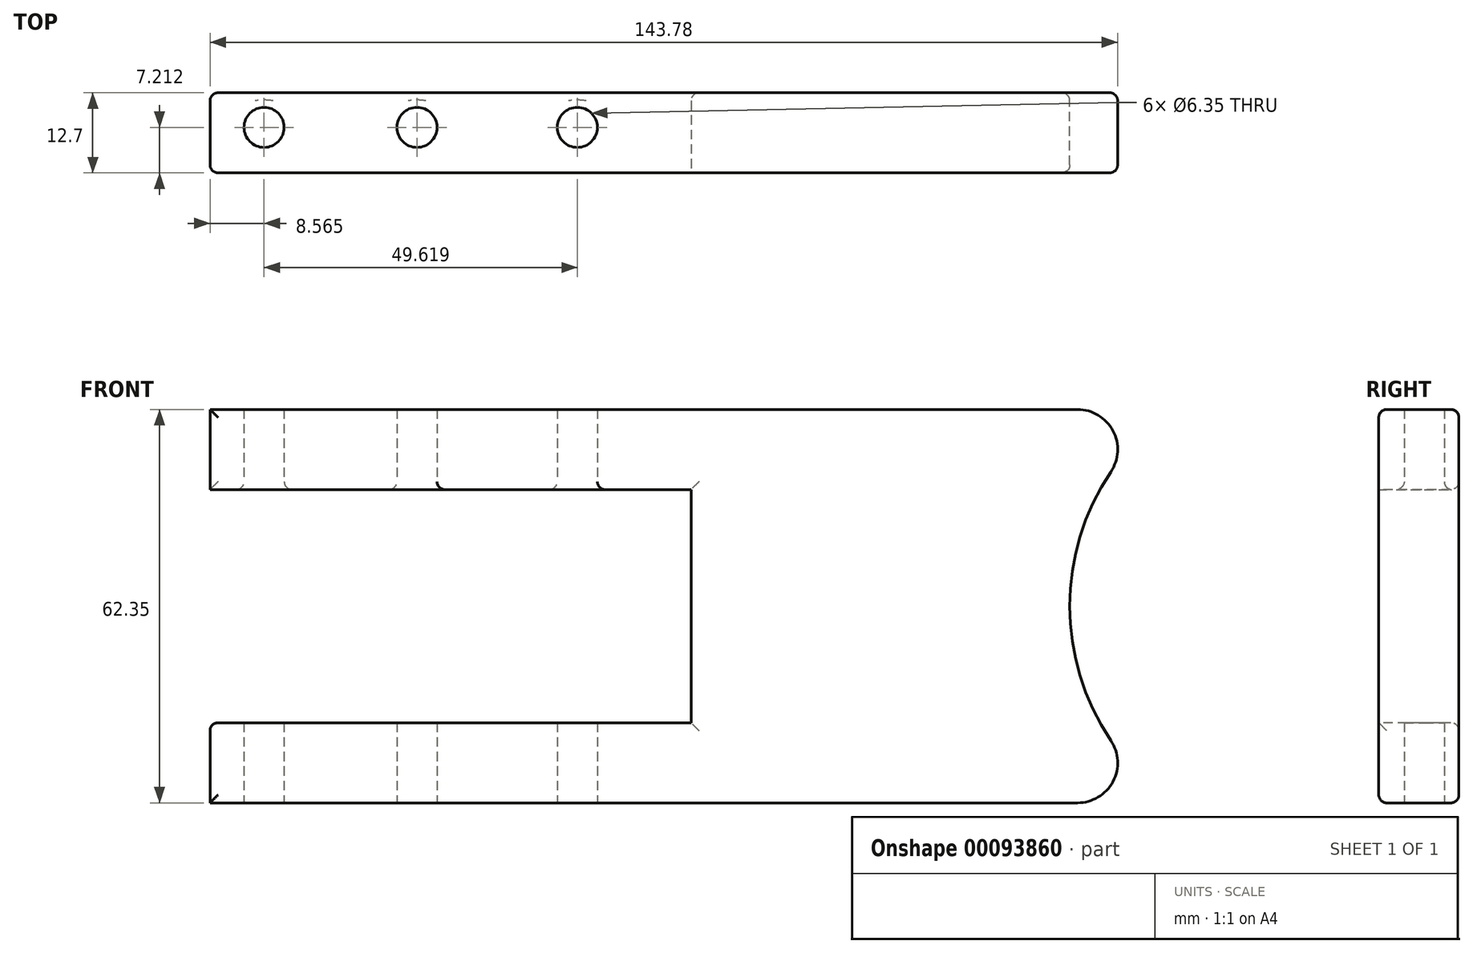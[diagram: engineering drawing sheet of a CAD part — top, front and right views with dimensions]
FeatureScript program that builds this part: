
annotation { "Feature Type Name" : "Feature", "Feature Type Description" : "" }
export const myFeature = defineFeature(function(context is Context, id is Id, definition is map)
    precondition{}
    {
        {
            var Q0;
            Q0=qCreatedBy(makeId("Front.planeOp"),FACE);
            var sketch = newSketch(context, id + "F0", { "sketchPlane" : qUnion([Q0])});
            skLineSegment(sketch, "E0.bottom", {"start": v(0, 62.35) * mm, "end": v(152.4, 62.35) * mm});
            skLineSegment(sketch, "E0.top", {"start": v(0, 0) * mm, "end": v(152.4, 0) * mm});
            skLineSegment(sketch, "E0.left", {"start": v(0, 62.35) * mm, "end": v(0, 0) * mm});
            skArc(sketch, "E1", {"start": v(152.4, 62.35) * mm, "mid": v(136.2, 31.18) * mm, "end": v(152.4, 0) * mm});
            skSolve(sketch);
        }
        {
            var Q0;
            Q0 = qSketchRegion(id + "F0", true);
            extrude(context, id + "F1", {"entities" : qUnion([Q0]), "depth" : 12.7 * mm});
        }
        {
            var Q0;
            Q0=makeQuery(id+"F1.opExtrude","SWEPT_EDGE",EDGE,{"disambiguationData":[OSD([sQuery(id+"F0.wireOp",EDGE,"E0.bottom"),sQuery(id+"F0.wireOp",EDGE,"E1")])]});
            var Q1;
            Q1=makeQuery(id+"F1.opExtrude","SWEPT_EDGE",EDGE,{"disambiguationData":[OSD([sQuery(id+"F0.wireOp",EDGE,"E0.top"),sQuery(id+"F0.wireOp",EDGE,"E1")])]});
            fillet(context, id + "F2", {"entities" : qUnion([Q0, Q1]), "radius" : 6.35 * mm, "tangentPropagation" : true, "allowEdgeOverflow" : false});
        }
        {
            var Q0;
            Q0=makeQuery(id+"F1.opExtrude","CAP_FACE",FACE,{"disambiguationData":[OSD([sQuery(id+"F0.wireOp",EDGE,"E0.bottom"),sQuery(id+"F0.wireOp",EDGE,"E0.top"),sQuery(id+"F0.wireOp",EDGE,"E0.left"),sQuery(id+"F0.wireOp",EDGE,"E1")])],"isStart":false});
            var sketch = newSketch(context, id + "F3", { "sketchPlane" : qUnion([Q0])});
            skLineSegment(sketch, "E2", {"start": v(0, 62.35) * mm, "end": v(0, 49.65) * mm});
            skLineSegment(sketch, "E3", {"start": v(0, 0) * mm, "end": v(0, 12.7) * mm});
            skLineSegment(sketch, "E4.bottom", {"start": v(0, 49.65) * mm, "end": v(76.2, 49.65) * mm});
            skLineSegment(sketch, "E4.top", {"start": v(0, 12.7) * mm, "end": v(76.2, 12.7) * mm});
            skLineSegment(sketch, "E4.left", {"start": v(0, 49.65) * mm, "end": v(0, 12.7) * mm});
            skLineSegment(sketch, "E4.right", {"start": v(76.2, 49.65) * mm, "end": v(76.2, 12.7) * mm});
            skSolve(sketch);
        }
        {
            var Q0;
            Q0=makeQuery(id+"F3.imprint","IMPRINT",FACE,{"disambiguationData":[TD([[makeQuery(id+"F3.imprint","IMPRINT",EDGE,{"derivedFrom":sQuery(id+"F3.wireOp",EDGE,"E4.bottom")}),-1.0]])]});
            extrude(context, id + "F4", {"entities" : qUnion([Q0]), "operationType" : NewBodyOperationType.REMOVE, "endBound" : BoundingType.THROUGH_ALL, "oppositeDirection" : true, "depth" : 25.4 * mm});
        }
        {
            var Q0;
            Q0=makeQuery(id+"F1.opExtrude","SWEPT_FACE",FACE,{"disambiguationData":[OSD([sQuery(id+"F0.wireOp",EDGE,"E0.top")])]});
            var sketch = newSketch(context, id + "F5", { "sketchPlane" : qUnion([Q0])});
            skCircle(sketch, "E5", {"center": v(8.57, 5.49) * mm, "radius": 3.18 * mm});
            skCircle(sketch, "E6", {"center": v(32.78, 5.49) * mm, "radius": 3.18 * mm});
            skCircle(sketch, "E7", {"center": v(58.18, 5.49) * mm, "radius": 3.18 * mm});
            skSolve(sketch);
        }
        {
            var Q0;
            Q0=makeQuery(id+"F5.imprint","IMPRINT",FACE,{"disambiguationData":[TD([[makeQuery(id+"F5.imprint","IMPRINT",EDGE,{"derivedFrom":sQuery(id+"F5.wireOp",EDGE,"E7")}),1.0]])]});
            var Q1;
            Q1=makeQuery(id+"F5.imprint","IMPRINT",FACE,{"disambiguationData":[TD([[makeQuery(id+"F5.imprint","IMPRINT",EDGE,{"derivedFrom":sQuery(id+"F5.wireOp",EDGE,"E6")}),1.0]])]});
            var Q2;
            Q2=makeQuery(id+"F5.imprint","IMPRINT",FACE,{"disambiguationData":[TD([[makeQuery(id+"F5.imprint","IMPRINT",EDGE,{"derivedFrom":sQuery(id+"F5.wireOp",EDGE,"E5")}),1.0]])]});
            extrude(context, id + "F6", {"entities" : qUnion([Q0, Q1, Q2]), "operationType" : NewBodyOperationType.REMOVE, "endBound" : BoundingType.THROUGH_ALL, "oppositeDirection" : true, "depth" : 25.4 * mm});
        }
        {
            var Q0;
            Q0=makeQuery(id+"F1.opExtrude","CAP_EDGE",EDGE,{"disambiguationData":[OSD([sQuery(id+"F0.wireOp",EDGE,"E0.bottom")])],"isStart":false});
            var Q1;
            Q1=makeQuery(id+"F6.boolean.opBoolean","COPY",EDGE,{"derivedFrom":makeQuery(id+"F6.opExtrude","CAP_EDGE",EDGE,{"disambiguationData":[OSD([sQuery(id+"F5.wireOp",EDGE,"E7")])],"isStart":true})});
            var Q2;
            Q2=makeQuery(id+"F6.boolean.opBoolean","COPY",EDGE,{"derivedFrom":makeQuery(id+"F6.opExtrude","CAP_EDGE",EDGE,{"disambiguationData":[OSD([sQuery(id+"F5.wireOp",EDGE,"E6")])],"isStart":true})});
            var Q3;
            Q3=makeQuery(id+"F6.boolean.opBoolean","COPY",EDGE,{"derivedFrom":makeQuery(id+"F6.opExtrude","CAP_EDGE",EDGE,{"disambiguationData":[OSD([sQuery(id+"F5.wireOp",EDGE,"E5")])],"isStart":true})});
            var Q4;
            Q4=makeQuery(id+"F6.boolean.opBoolean","INTERSECT",EDGE,{"derivedFrom":[makeQuery(id+"F4.boolean.opBoolean","COPY",FACE,{"derivedFrom":makeQuery(id+"F4.opExtrude","SWEPT_FACE",FACE,{"disambiguationData":[OSD([sQuery(id+"F3.wireOp",EDGE,"E4.bottom")])]})}),makeQuery(id+"F6.opExtrude","SWEPT_FACE",FACE,{"disambiguationData":[OSD([sQuery(id+"F5.wireOp",EDGE,"E7")])]})]});
            var Q5;
            Q5=makeQuery(id+"F6.boolean.opBoolean","INTERSECT",EDGE,{"derivedFrom":[makeQuery(id+"F4.boolean.opBoolean","COPY",FACE,{"derivedFrom":makeQuery(id+"F4.opExtrude","SWEPT_FACE",FACE,{"disambiguationData":[OSD([sQuery(id+"F3.wireOp",EDGE,"E4.bottom")])]})}),makeQuery(id+"F6.opExtrude","SWEPT_FACE",FACE,{"disambiguationData":[OSD([sQuery(id+"F5.wireOp",EDGE,"E6")])]})]});
            var Q6;
            Q6=makeQuery(id+"F6.boolean.opBoolean","INTERSECT",EDGE,{"derivedFrom":[makeQuery(id+"F4.boolean.opBoolean","COPY",FACE,{"derivedFrom":makeQuery(id+"F4.opExtrude","SWEPT_FACE",FACE,{"disambiguationData":[OSD([sQuery(id+"F3.wireOp",EDGE,"E4.bottom")])]})}),makeQuery(id+"F6.opExtrude","SWEPT_FACE",FACE,{"disambiguationData":[OSD([sQuery(id+"F5.wireOp",EDGE,"E5")])]})]});
            var Q7;
            Q7=makeQuery(id+"F4.boolean.opBoolean","COPY",EDGE,{"derivedFrom":makeQuery(id+"F4.opExtrude","CAP_EDGE",EDGE,{"disambiguationData":[OSD([sQuery(id+"F3.wireOp",EDGE,"E4.bottom")])],"isStart":true})});
            var Q8;
            Q8=makeQuery(id+"F4.boolean.opBoolean","COPY",EDGE,{"derivedFrom":makeQuery(id+"F4.opExtrude","CAP_EDGE",EDGE,{"disambiguationData":[OSD([sQuery(id+"F3.wireOp",EDGE,"E4.right")])],"isStart":true})});
            var Q9;
            Q9=makeQuery(id+"F4.boolean.opBoolean","COPY",EDGE,{"derivedFrom":makeQuery(id+"F4.opExtrude","CAP_EDGE",EDGE,{"disambiguationData":[OSD([sQuery(id+"F3.wireOp",EDGE,"E4.top")])],"isStart":true})});
            var Q10;
            {var subQ0=sQuery(id+"F0.wireOp",EDGE,"E0.bottom");var subQ1=sQuery(id+"F0.wireOp",EDGE,"E0.left");Q10=makeQuery(id+"F4.boolean.opBoolean","SPLIT",EDGE,{"disambiguationData":[TD([makeQuery(id+"F1.opExtrude","SWEPT_FACE",FACE,{"disambiguationData":[OSD([subQ0])]})])],"derivedFrom":makeQuery(id+"F1.opExtrude","CAP_EDGE",EDGE,{"disambiguationData":[OSD([subQ1])],"isStart":false})});}
            var Q11;
            {var subQ0=sQuery(id+"F0.wireOp",EDGE,"E0.left");var subQ1=sQuery(id+"F0.wireOp",EDGE,"E0.top");Q11=makeQuery(id+"F4.boolean.opBoolean","SPLIT",EDGE,{"disambiguationData":[TD([makeQuery(id+"F1.opExtrude","SWEPT_FACE",FACE,{"disambiguationData":[OSD([subQ1])]})])],"derivedFrom":makeQuery(id+"F1.opExtrude","CAP_EDGE",EDGE,{"disambiguationData":[OSD([subQ0])],"isStart":false})});}
            var Q12;
            Q12=makeQuery(id+"F1.opExtrude","CAP_EDGE",EDGE,{"disambiguationData":[OSD([sQuery(id+"F0.wireOp",EDGE,"E0.top")])],"isStart":true});
            var Q13;
            Q13=makeQuery(id+"F4.boolean.opBoolean","COPY",EDGE,{"derivedFrom":makeQuery(id+"F4.opExtrude","SWEPT_EDGE",EDGE,{"disambiguationData":[OSD([sQuery(id+"F3.wireOp",EDGE,"E3"),sQuery(id+"F3.wireOp",EDGE,"E4.top"),sQuery(id+"F3.wireOp",EDGE,"E4.left")])]})});
            var Q14;
            Q14=makeQuery(id+"F4.boolean.opBoolean","INTERSECT",EDGE,{"derivedFrom":[makeQuery(id+"F1.opExtrude","CAP_FACE",FACE,{"disambiguationData":[OSD([sQuery(id+"F0.wireOp",EDGE,"E0.bottom"),sQuery(id+"F0.wireOp",EDGE,"E0.top"),sQuery(id+"F0.wireOp",EDGE,"E0.left"),sQuery(id+"F0.wireOp",EDGE,"E1")])],"isStart":true}),makeQuery(id+"F4.opExtrude","SWEPT_FACE",FACE,{"disambiguationData":[OSD([sQuery(id+"F3.wireOp",EDGE,"E4.top")])]})]});
            var Q15;
            Q15=makeQuery(id+"F4.boolean.opBoolean","INTERSECT",EDGE,{"derivedFrom":[makeQuery(id+"F1.opExtrude","CAP_FACE",FACE,{"disambiguationData":[OSD([sQuery(id+"F0.wireOp",EDGE,"E0.bottom"),sQuery(id+"F0.wireOp",EDGE,"E0.top"),sQuery(id+"F0.wireOp",EDGE,"E0.left"),sQuery(id+"F0.wireOp",EDGE,"E1")])],"isStart":true}),makeQuery(id+"F4.opExtrude","SWEPT_FACE",FACE,{"disambiguationData":[OSD([sQuery(id+"F3.wireOp",EDGE,"E4.right")])]})]});
            var Q16;
            Q16=makeQuery(id+"F4.boolean.opBoolean","INTERSECT",EDGE,{"derivedFrom":[makeQuery(id+"F1.opExtrude","CAP_FACE",FACE,{"disambiguationData":[OSD([sQuery(id+"F0.wireOp",EDGE,"E0.bottom"),sQuery(id+"F0.wireOp",EDGE,"E0.top"),sQuery(id+"F0.wireOp",EDGE,"E0.left"),sQuery(id+"F0.wireOp",EDGE,"E1")])],"isStart":true}),makeQuery(id+"F4.opExtrude","SWEPT_FACE",FACE,{"disambiguationData":[OSD([sQuery(id+"F3.wireOp",EDGE,"E4.bottom")])]})]});
            var Q17;
            {var subQ0=sQuery(id+"F0.wireOp",EDGE,"E0.left");var subQ1=sQuery(id+"F0.wireOp",EDGE,"E0.top");Q17=makeQuery(id+"F4.boolean.opBoolean","SPLIT",EDGE,{"disambiguationData":[TD([makeQuery(id+"F1.opExtrude","SWEPT_FACE",FACE,{"disambiguationData":[OSD([subQ1])]})])],"derivedFrom":makeQuery(id+"F1.opExtrude","CAP_EDGE",EDGE,{"disambiguationData":[OSD([subQ0])],"isStart":true})});}
            var Q18;
            {var subQ0=sQuery(id+"F0.wireOp",EDGE,"E0.bottom");var subQ1=sQuery(id+"F0.wireOp",EDGE,"E0.left");Q18=makeQuery(id+"F4.boolean.opBoolean","SPLIT",EDGE,{"disambiguationData":[TD([makeQuery(id+"F1.opExtrude","SWEPT_FACE",FACE,{"disambiguationData":[OSD([subQ0])]})])],"derivedFrom":makeQuery(id+"F1.opExtrude","CAP_EDGE",EDGE,{"disambiguationData":[OSD([subQ1])],"isStart":true})});}
            fillet(context, id + "F7", {"entities" : qUnion([Q0, Q1, Q2, Q3, Q4, Q5, Q6, Q7, Q8, Q9, Q10, Q11, Q12, Q13, Q14, Q15, Q16, Q17, Q18]), "radius" : 1.27 * mm, "tangentPropagation" : true, "allowEdgeOverflow" : false});
        }
    });
